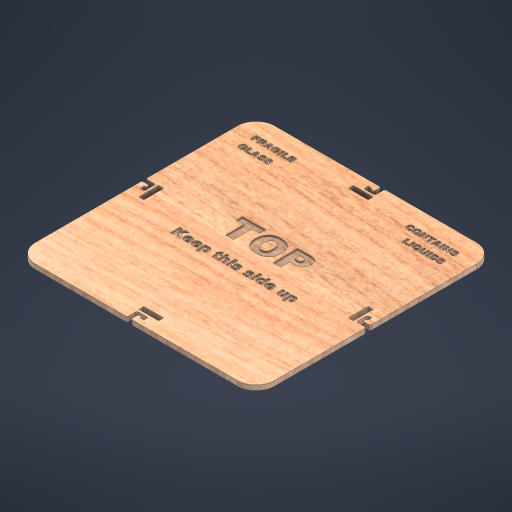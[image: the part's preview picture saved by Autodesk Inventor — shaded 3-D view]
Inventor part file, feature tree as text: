
AUTODESK INVENTOR PART (.ipt)
format: ipt  version: 2024.1 (Build 281209000, 209)  size: 1,412,096 bytes
history: native  units: mm
features: extrude x3, sketch x3, fillet x1
ambient origin geometry x8: Origin, YZ Plane, XZ Plane, XY Plane, X Axis, Y Axis, Z Axis, Center Point
bodies: Solid1 (feature_tree)
feature tree (7):
  extrude  "Extrusion1"  Depth=6.0mm
  fillet  "Fillet1"  Radius=3.0mm
  extrude  "Extrusion2"  Depth=3.0mm
  extrude  "Extrusion3"  Depth=40.0mm TaperAngle=360.0deg
  sketch  "Sketch1"  dims[d16=15.0mm d17=6.0mm d18=3.0mm]
  sketch  "Sketch2"  dims[d19=6.0mm d20=3.0mm]
  sketch  "Sketch3"  dims[d21=1.5mm d22=40.0mm d24=360.0deg d26=4.0mm d27=0.0mm d28=1.5mm d29=4.0mm d30=16.0mm d31=83.0mm d32=2.0mm d33=194.0mm d34=194.0mm d35=40.0mm d37=360.0deg d39=15.0mm d40=130.0mm d41=75.0mm d42=30.0mm d43=5.0mm d44=1.0mm d45=0.0mm d46=45.0mm d47=20.0mm d48=40.0mm d49=20.0mm d50=1.0mm d51=0.0mm]
